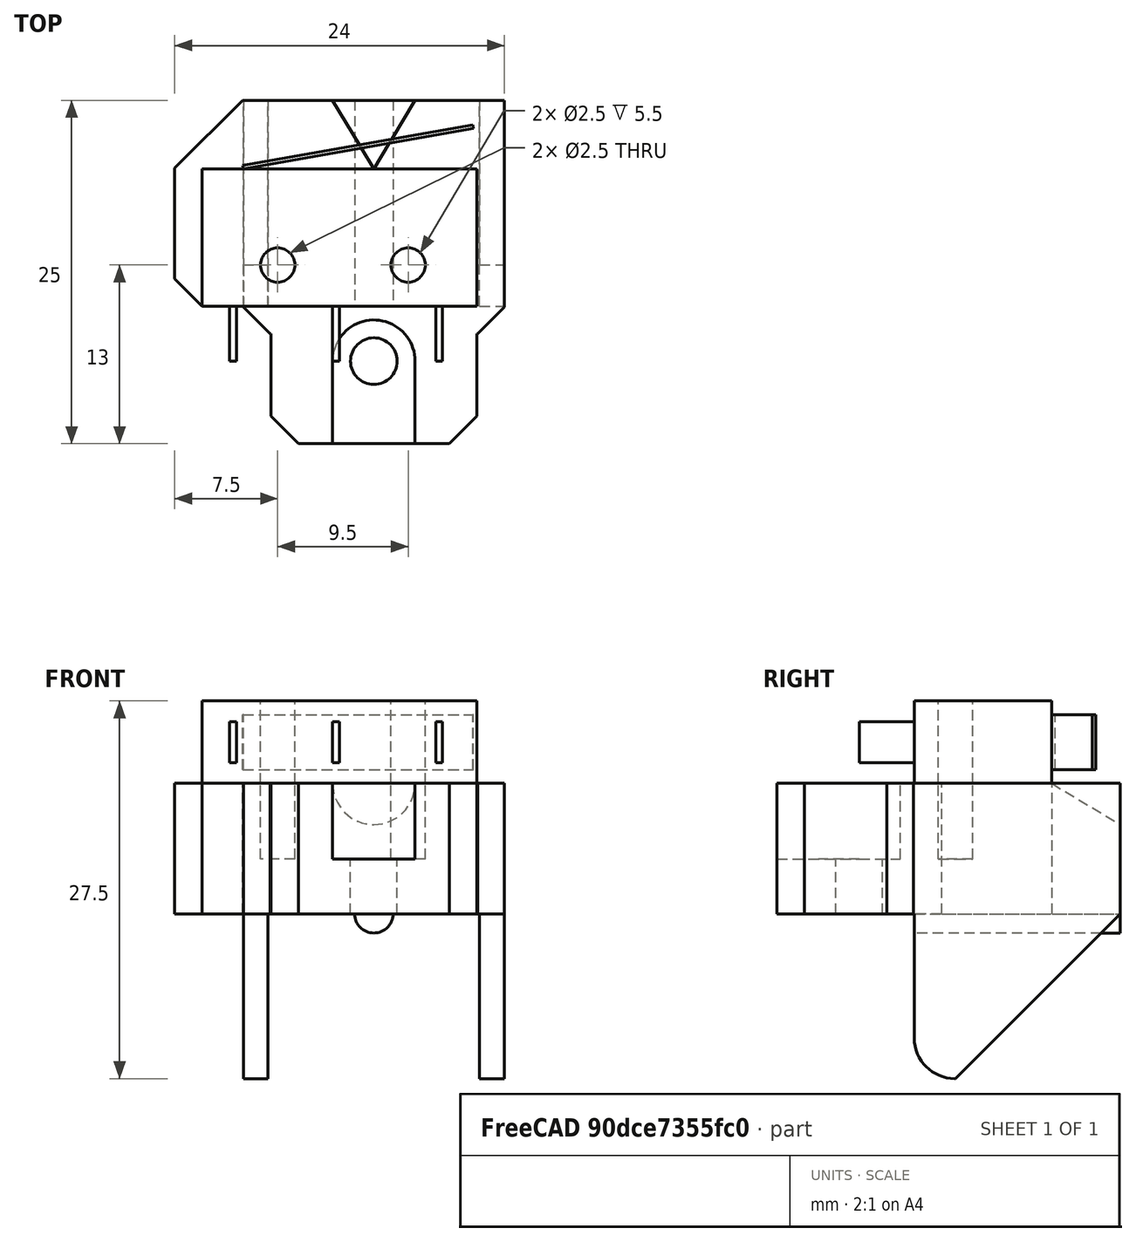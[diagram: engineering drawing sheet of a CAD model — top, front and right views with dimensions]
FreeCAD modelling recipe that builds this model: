
FCSTD DOCUMENT  (FreeCAD 0.14R3700 (Git))
Label: Igus-Endstop
License: CC-BY 3.0
LicenseURL: http://creativecommons.org/licenses/by/3.0/
objects: Part::Box×14, Part::Cylinder×7, Part::MultiFuse×4, Part::Cut×3, Part::Cone×1, Part::Chamfer×1, Part::Fillet×1
note: 31 computed .brp shape members not serialized (recipe doc carries the construction recipe); baked Part::Feature solids carry a one-line shape summary decoded from their .brp

FEATURE [Part::Box] Box002  label="Cube002"
  Height = 6
  Length = 20
  Width = 10
FEATURE [Part::Cylinder] Cylinder
  Angle = 360
  Height = 6
  Placement = pos=(15,3,0) rot=(0,0,1;0rad)
  Radius = 1.25
FEATURE [Part::Cylinder] Cylinder001
  Angle = 360
  Height = 6
  Placement = pos=(5.5,3,0) rot=(0,0,1;0rad)
  Radius = 1.25
FEATURE [Part::Box] Box003  label="Cube003"
  Height = 3
  Length = 0.5
  Placement = pos=(17,-4,1.5) rot=(0,0,1;0rad)
  Width = 4
FEATURE [Part::Box] Box004  label="Cube004"
  Height = 3
  Length = 0.5
  Placement = pos=(9.5,-4,1.5) rot=(0,0,1;0rad)
  Width = 4
FEATURE [Part::Box] Box005  label="Cube005"
  Height = 3
  Length = 0.5
  Placement = pos=(2,-4,1.5) rot=(0,0,1;0rad)
  Width = 4
FEATURE [Part::Box] Box006  label="Cube006"
  Height = 4
  Length = 17
  Placement = pos=(3,10,1) rot=(0,0,1;0.174533rad)
  Width = 0.25
FEATURE [Part::MultiFuse] Fusion
  Shapes = -> [Box002,Box003,Box004,Box005,Box006]
FEATURE [Part::Cut] Cut
  Base = -> Fusion
  Tool = -> Cylinder
FEATURE [Part::Cut] Cut001  label="DO_NOT_PRINT-Microswitch"
  Base = -> Cut
  Placement = pos=(-5,10,9.5) rot=(0,0,1;0rad)
  Tool = -> Cylinder001
FEATURE [Part::Box] Box007  label="Base"
  Height = 9.5
  Length = 15
  Width = 25
FEATURE [Part::Box] Box008  label="DeltaCube"
  Height = 5.5
  Length = 6
  Placement = pos=(4.5,0,4) rot=(0,0,1;0rad)
  Width = 6
FEATURE [Part::Cylinder] Cylinder002  label="DeltaCylinder"
  Angle = 360
  Height = 5.5
  Placement = pos=(7.5,6,4) rot=(0,0,1;0rad)
  Radius = 3
FEATURE [Part::Cylinder] Cylinder003  label="DeltaM3"
  Angle = 360
  Height = 9.5
  Placement = pos=(7.5,6,0) rot=(0,0,1;0rad)
  Radius = 1.7
FEATURE [Part::Box] Box009  label="AttachRight"
  Height = 9.5
  Length = 5
  Placement = pos=(-7,10,0) rot=(0,0,1;0rad)
  Width = 15
FEATURE [Part::Box] Box010  label="SideLeft"
  Height = 21.5
  Length = 1.8
  Placement = pos=(15.2,10,-12) rot=(0,0,1;0rad)
  Width = 15
FEATURE [Part::Box] Box011  label="SideRight"
  Height = 21.5
  Length = 1.8
  Placement = pos=(-2,10,-12) rot=(0,0,1;0rad)
  Width = 15
FEATURE [Part::Box] Box012  label="SideLeftDistance"
  Height = 9.5
  Length = 0.2
  Placement = pos=(15,10,0) rot=(0,0,1;0rad)
  Width = 15
FEATURE [Part::Box] Box013  label="SideRightDistance"
  Height = 9.5
  Length = 0.2
  Placement = pos=(-0.2,10,0) rot=(0,0,1;0rad)
  Width = 15
FEATURE [Part::Cylinder] Cylinder004  label="SnapToExtrusion"
  Angle = 360
  Height = 15
  Placement = pos=(7.5,25,0) rot=(1,0,0;1.5708rad)
  Radius = 1.4
FEATURE [Part::Cylinder] Cylinder005  label="DeltaM2.5-1"
  Angle = 360
  Height = 6
  Placement = pos=(10,13,4) rot=(0,0,1;0rad)
  Radius = 1.25
FEATURE [Part::Cylinder] Cylinder006  label="DeltaM2.5-2"
  Angle = 360
  Height = 6
  Placement = pos=(0.5,13,4) rot=(0,0,1;0rad)
  Radius = 1.25
FEATURE [Part::MultiFuse] Fusion001  label="DeltaNutPocket"
  Shapes = -> [Box008,Cylinder002]
FEATURE [Part::Cone] Cone  label="DeltaAdjustmentScrew"
  Angle = 360
  Height = 5
  Placement = pos=(7.5,20,9.5) rot=(-1,0,0;1.5708rad)
  Radius1 = 0
  Radius2 = 3
FEATURE [Part::Box] Box  label="Cube"
  Height = 9.5
  Length = 2
  Placement = pos=(-2,8,0) rot=(0,0,1;0rad)
  Width = 2
FEATURE [Part::Box] Box014  label="Cube007"
  Height = 9.5
  Length = 2
  Placement = pos=(15,8,0) rot=(0,0,1;0rad)
  Width = 2
FEATURE [Part::MultiFuse] Fusion002
  Shapes = -> [Box007,Box014,Box,Box011,Box010,Cylinder004,Box013,Box012,Box009]
FEATURE [Part::MultiFuse] Fusion003  label="DeltaFusion"
  Shapes = -> [Cylinder006,Cone,Cylinder003,Fusion001,Cylinder005]
FEATURE [Part::Cut] Cut002
  Base = -> Fusion002
  Tool = -> Fusion003
FEATURE [Part::Chamfer] Chamfer
  Base = -> Cut002
  Edges = 8 edges: [Edge1 r=2,Edge3 r=4.95,Edge13 r=1.95,Edge21 r=12,Edge52 r=2,Edge80 r=2,Edge115 r=1.95,Edge124 r=12]
FEATURE [Part::Fillet] Fillet  label="Igus-Endstop"
  Base = -> Chamfer
  Edges = 2 edges r=2.95: [Edge46,Edge139]
